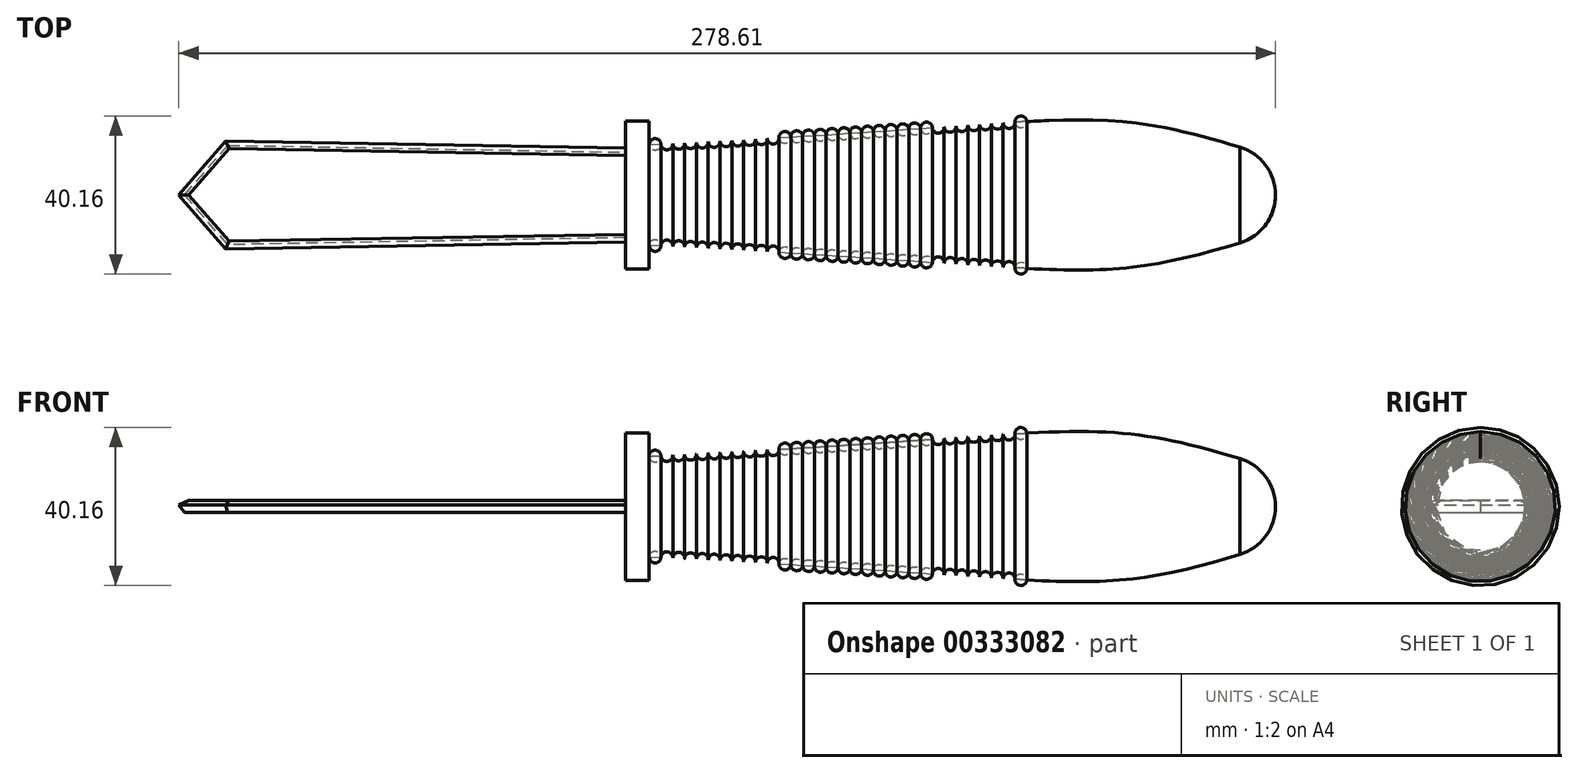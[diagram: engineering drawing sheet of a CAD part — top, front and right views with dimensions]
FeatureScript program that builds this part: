
annotation { "Feature Type Name" : "Feature", "Feature Type Description" : "" }
export const myFeature = defineFeature(function(context is Context, id is Id, definition is map)
    precondition{}
    {
        {
            var Q0;
            Q0=qCreatedBy(makeId("Top.planeOp"),FACE);
            var sketch = newSketch(context, id + "F0", { "sketchPlane" : qUnion([Q0])});
            skLineSegment(sketch, "E0", {"start": v(0, 0) * mm, "end": v(0, -18.75) * mm});
            skLineSegment(sketch, "E1", {"start": v(0, -18.75) * mm, "end": v(6, -18.75) * mm});
            skLineSegment(sketch, "E2", {"start": v(6, -18.75) * mm, "end": v(6, -12.75) * mm});
            skArc(sketch, "E3", {"start": v(156.05, -12.16) * mm, "mid": v(162.59, -7.58) * mm, "end": v(165.1, 0) * mm});
            skFitSpline(sketch, "E4", {"points": [v(6, -12.75) * mm, v(156.05, -12.16) * mm, v(257.66, 24.42) * mm], "startDerivative": vector(616.47, -30.16) * mm, "endDerivative": vector(40.55, 25.58) * mm});
            skLineSegment(sketch, "E5", {"start": v(0, 0) * mm, "end": v(152.4, 0) * mm});
            skCircle(sketch, "E6", {"center": v(7.5, -12.82) * mm, "radius": 1.5 * mm});
            skCircle(sketch, "E7", {"center": v(10.5, -12.97) * mm, "radius": 1.5 * mm});
            skCircle(sketch, "E8", {"center": v(13.5, -13.13) * mm, "radius": 1.5 * mm});
            skCircle(sketch, "E9", {"center": v(16.5, -13.28) * mm, "radius": 1.5 * mm});
            skCircle(sketch, "E10", {"center": v(19.5, -13.44) * mm, "radius": 1.5 * mm});
            skCircle(sketch, "E11", {"center": v(22.5, -13.6) * mm, "radius": 1.5 * mm});
            skLineSegment(sketch, "E12", {"start": v(152.4, 0) * mm, "end": v(165.1, 0) * mm});
            skLineSegment(sketch, "E13", {"start": v(7.5, -12.82) * mm, "end": v(10.5, -12.97) * mm, "construction": true});
            skLineSegment(sketch, "E14", {"start": v(10.5, -12.97) * mm, "end": v(13.5, -13.13) * mm, "construction": true});
            skLineSegment(sketch, "E15", {"start": v(13.5, -13.13) * mm, "end": v(16.5, -13.28) * mm, "construction": true});
            skLineSegment(sketch, "E16", {"start": v(16.5, -13.28) * mm, "end": v(19.5, -13.44) * mm, "construction": true});
            skLineSegment(sketch, "E17", {"start": v(19.5, -13.44) * mm, "end": v(22.5, -13.6) * mm, "construction": true});
            skCircle(sketch, "E18", {"center": v(28.5, -13.93) * mm, "radius": 1.5 * mm});
            skCircle(sketch, "E19", {"center": v(31.5, -14.1) * mm, "radius": 1.5 * mm});
            skCircle(sketch, "E20", {"center": v(25.5, -13.77) * mm, "radius": 1.5 * mm});
            skCircle(sketch, "E21", {"center": v(34.5, -14.28) * mm, "radius": 1.5 * mm});
            skCircle(sketch, "E22", {"center": v(37.5, -14.45) * mm, "radius": 1.5 * mm});
            skCircle(sketch, "E23", {"center": v(40.49, -14.63) * mm, "radius": 1.5 * mm});
            skCircle(sketch, "E24", {"center": v(43.49, -14.82) * mm, "radius": 1.5 * mm});
            skCircle(sketch, "E25", {"center": v(46.49, -15) * mm, "radius": 1.5 * mm});
            skCircle(sketch, "E26", {"center": v(49.48, -15.2) * mm, "radius": 1.5 * mm});
            skCircle(sketch, "E27", {"center": v(52.48, -15.38) * mm, "radius": 1.5 * mm});
            skCircle(sketch, "E28", {"center": v(55.48, -15.58) * mm, "radius": 1.5 * mm});
            skLineSegment(sketch, "E29", {"start": v(22.5, -13.6) * mm, "end": v(25.5, -13.77) * mm, "construction": true});
            skLineSegment(sketch, "E30", {"start": v(25.5, -13.77) * mm, "end": v(28.5, -13.93) * mm, "construction": true});
            skLineSegment(sketch, "E31", {"start": v(28.5, -13.93) * mm, "end": v(31.5, -14.1) * mm, "construction": true});
            skLineSegment(sketch, "E32", {"start": v(31.5, -14.1) * mm, "end": v(34.5, -14.28) * mm, "construction": true});
            skLineSegment(sketch, "E33", {"start": v(34.5, -14.28) * mm, "end": v(37.5, -14.45) * mm, "construction": true});
            skLineSegment(sketch, "E34", {"start": v(37.5, -14.45) * mm, "end": v(40.49, -14.63) * mm, "construction": true});
            skLineSegment(sketch, "E35", {"start": v(40.49, -14.63) * mm, "end": v(43.49, -14.82) * mm, "construction": true});
            skLineSegment(sketch, "E36", {"start": v(43.49, -14.82) * mm, "end": v(46.49, -15) * mm, "construction": true});
            skLineSegment(sketch, "E37", {"start": v(52.48, -15.38) * mm, "end": v(55.48, -15.58) * mm, "construction": true});
            skLineSegment(sketch, "E38", {"start": v(52.48, -15.38) * mm, "end": v(49.48, -15.2) * mm, "construction": true});
            skLineSegment(sketch, "E39", {"start": v(49.48, -15.2) * mm, "end": v(46.49, -15) * mm, "construction": true});
            skCircle(sketch, "E40", {"center": v(58.48, -15.77) * mm, "radius": 1.5 * mm});
            skCircle(sketch, "E41", {"center": v(61.47, -15.97) * mm, "radius": 1.5 * mm});
            skCircle(sketch, "E42", {"center": v(64.47, -16.18) * mm, "radius": 1.5 * mm});
            skCircle(sketch, "E43", {"center": v(67.47, -16.38) * mm, "radius": 1.5 * mm});
            skCircle(sketch, "E44", {"center": v(70.46, -16.59) * mm, "radius": 1.5 * mm});
            skLineSegment(sketch, "E45", {"start": v(55.48, -15.58) * mm, "end": v(58.48, -15.77) * mm, "construction": true});
            skLineSegment(sketch, "E46", {"start": v(58.48, -15.77) * mm, "end": v(61.47, -15.97) * mm, "construction": true});
            skLineSegment(sketch, "E47", {"start": v(61.47, -15.97) * mm, "end": v(64.47, -16.18) * mm, "construction": true});
            skLineSegment(sketch, "E48", {"start": v(64.47, -16.18) * mm, "end": v(67.47, -16.38) * mm, "construction": true});
            skLineSegment(sketch, "E49", {"start": v(67.47, -16.38) * mm, "end": v(70.46, -16.59) * mm, "construction": true});
            skCircle(sketch, "E50", {"center": v(73.46, -16.8) * mm, "radius": 1.5 * mm});
            skCircle(sketch, "E51", {"center": v(76.46, -17) * mm, "radius": 1.5 * mm});
            skCircle(sketch, "E52", {"center": v(79.45, -17.21) * mm, "radius": 1.5 * mm});
            skCircle(sketch, "E53", {"center": v(82.45, -17.42) * mm, "radius": 1.5 * mm});
            skCircle(sketch, "E54", {"center": v(85.45, -17.63) * mm, "radius": 1.5 * mm});
            skCircle(sketch, "E55", {"center": v(88.44, -17.83) * mm, "radius": 1.5 * mm});
            skCircle(sketch, "E56", {"center": v(91.44, -18.03) * mm, "radius": 1.5 * mm});
            skCircle(sketch, "E57", {"center": v(94.44, -18.22) * mm, "radius": 1.5 * mm});
            skLineSegment(sketch, "E58", {"start": v(70.46, -16.59) * mm, "end": v(73.46, -16.8) * mm, "construction": true});
            skLineSegment(sketch, "E59", {"start": v(73.46, -16.8) * mm, "end": v(76.46, -17) * mm, "construction": true});
            skLineSegment(sketch, "E60", {"start": v(76.46, -17) * mm, "end": v(79.45, -17.21) * mm, "construction": true});
            skLineSegment(sketch, "E61", {"start": v(79.45, -17.21) * mm, "end": v(82.45, -17.42) * mm, "construction": true});
            skLineSegment(sketch, "E62", {"start": v(82.45, -17.42) * mm, "end": v(85.45, -17.63) * mm, "construction": true});
            skLineSegment(sketch, "E63", {"start": v(85.45, -17.63) * mm, "end": v(88.44, -17.83) * mm, "construction": true});
            skLineSegment(sketch, "E64", {"start": v(88.44, -17.83) * mm, "end": v(91.44, -18.03) * mm, "construction": true});
            skLineSegment(sketch, "E65", {"start": v(91.44, -18.03) * mm, "end": v(94.44, -18.22) * mm, "construction": true});
            skCircle(sketch, "E66", {"center": v(97.44, -18.4) * mm, "radius": 1.5 * mm});
            skCircle(sketch, "E67", {"center": v(100.43, -18.58) * mm, "radius": 1.5 * mm});
            skLineSegment(sketch, "E68", {"start": v(94.44, -18.22) * mm, "end": v(97.44, -18.4) * mm, "construction": true});
            skLineSegment(sketch, "E69", {"start": v(97.44, -18.4) * mm, "end": v(100.43, -18.58) * mm, "construction": true});
            skSolve(sketch);
        }
        {
            var Q0;
            Q0=makeQuery(id+"F0.imprint","IMPRINT",FACE,{"disambiguationData":[TD([[makeQuery(id+"F0.imprint","IMPRINT",EDGE,{"derivedFrom":sQuery(id+"F0.wireOp",EDGE,"E0")}),1.0]])]});
            var Q1;
            {var subQ0=sQuery(id+"F0.wireOp",EDGE,"E10");var subQ1=sQuery(id+"F0.wireOp",EDGE,"E4");var subQ2=makeQuery(id+"F0.imprint","INTERSECT",VERTEX,{"disambiguationData":[OD(0.0)],"derivedFrom":[subQ1,subQ0]});Q1=makeQuery(id+"F0.imprint","IMPRINT",FACE,{"disambiguationData":[TD([[makeQuery(id+"F0.imprint","IMPRINT",EDGE,{"disambiguationData":[TD([[subQ2,-1.0]])],"derivedFrom":subQ1}),-1.0]])]});}
            var Q2;
            {var subQ0=sQuery(id+"F0.wireOp",EDGE,"E10");var subQ1=sQuery(id+"F0.wireOp",EDGE,"E4");var subQ2=makeQuery(id+"F0.imprint","INTERSECT",VERTEX,{"disambiguationData":[OD(0.0)],"derivedFrom":[subQ1,subQ0]});Q2=makeQuery(id+"F0.imprint","IMPRINT",FACE,{"disambiguationData":[TD([[makeQuery(id+"F0.imprint","IMPRINT",EDGE,{"disambiguationData":[TD([[subQ2,-1.0]])],"derivedFrom":subQ1}),1.0]])]});}
            var Q3;
            {var subQ0=sQuery(id+"F0.wireOp",EDGE,"E11");var subQ1=sQuery(id+"F0.wireOp",EDGE,"E4");var subQ2=makeQuery(id+"F0.imprint","INTERSECT",VERTEX,{"disambiguationData":[OD(0.0)],"derivedFrom":[subQ1,subQ0]});Q3=makeQuery(id+"F0.imprint","IMPRINT",FACE,{"disambiguationData":[TD([[makeQuery(id+"F0.imprint","IMPRINT",EDGE,{"disambiguationData":[TD([[subQ2,-1.0]])],"derivedFrom":subQ1}),-1.0]])]});}
            var Q4;
            {var subQ0=sQuery(id+"F0.wireOp",EDGE,"E9");var subQ1=sQuery(id+"F0.wireOp",EDGE,"E4");var subQ2=makeQuery(id+"F0.imprint","INTERSECT",VERTEX,{"disambiguationData":[OD(0.0)],"derivedFrom":[subQ1,subQ0]});Q4=makeQuery(id+"F0.imprint","IMPRINT",FACE,{"disambiguationData":[TD([[makeQuery(id+"F0.imprint","IMPRINT",EDGE,{"disambiguationData":[TD([[subQ2,-1.0]])],"derivedFrom":subQ1}),-1.0]])]});}
            var Q5;
            {var subQ0=sQuery(id+"F0.wireOp",EDGE,"E8");var subQ1=sQuery(id+"F0.wireOp",EDGE,"E4");var subQ2=makeQuery(id+"F0.imprint","INTERSECT",VERTEX,{"disambiguationData":[OD(0.0)],"derivedFrom":[subQ1,subQ0]});Q5=makeQuery(id+"F0.imprint","IMPRINT",FACE,{"disambiguationData":[TD([[makeQuery(id+"F0.imprint","IMPRINT",EDGE,{"disambiguationData":[TD([[subQ2,-1.0]])],"derivedFrom":subQ1}),-1.0]])]});}
            var Q6;
            {var subQ0=sQuery(id+"F0.wireOp",EDGE,"E6");var subQ2=sQuery(id+"F0.wireOp",EDGE,"E2");var subQ4=makeQuery(id+"F0.imprint","INTERSECT",VERTEX,{"derivedFrom":[subQ2,subQ0]});Q6=makeQuery(id+"F0.imprint","IMPRINT",FACE,{"disambiguationData":[TD([[makeQuery(id+"F0.imprint","IMPRINT",EDGE,{"disambiguationData":[TD([[subQ4,-1.0]])],"derivedFrom":subQ0}),1.0]])]});}
            var Q7;
            {var subQ0=sQuery(id+"F0.wireOp",EDGE,"E7");var subQ1=sQuery(id+"F0.wireOp",EDGE,"E4");var subQ2=makeQuery(id+"F0.imprint","INTERSECT",VERTEX,{"disambiguationData":[OD(0.0)],"derivedFrom":[subQ1,subQ0]});Q7=makeQuery(id+"F0.imprint","IMPRINT",FACE,{"disambiguationData":[TD([[makeQuery(id+"F0.imprint","IMPRINT",EDGE,{"disambiguationData":[TD([[subQ2,-1.0]])],"derivedFrom":subQ1}),-1.0]])]});}
            var Q8;
            {var subQ0=sQuery(id+"F0.wireOp",EDGE,"E20");var subQ1=sQuery(id+"F0.wireOp",EDGE,"E4");var subQ2=makeQuery(id+"F0.imprint","INTERSECT",VERTEX,{"disambiguationData":[OD(0.0)],"derivedFrom":[subQ1,subQ0]});Q8=makeQuery(id+"F0.imprint","IMPRINT",FACE,{"disambiguationData":[TD([[makeQuery(id+"F0.imprint","IMPRINT",EDGE,{"disambiguationData":[TD([[subQ2,-1.0]])],"derivedFrom":subQ1}),-1.0]])]});}
            var Q9;
            {var subQ0=sQuery(id+"F0.wireOp",EDGE,"E18");var subQ1=sQuery(id+"F0.wireOp",EDGE,"E4");var subQ2=makeQuery(id+"F0.imprint","INTERSECT",VERTEX,{"disambiguationData":[OD(0.0)],"derivedFrom":[subQ1,subQ0]});Q9=makeQuery(id+"F0.imprint","IMPRINT",FACE,{"disambiguationData":[TD([[makeQuery(id+"F0.imprint","IMPRINT",EDGE,{"disambiguationData":[TD([[subQ2,-1.0]])],"derivedFrom":subQ1}),-1.0]])]});}
            var Q10;
            {var subQ0=sQuery(id+"F0.wireOp",EDGE,"E19");var subQ1=sQuery(id+"F0.wireOp",EDGE,"E4");var subQ2=makeQuery(id+"F0.imprint","INTERSECT",VERTEX,{"disambiguationData":[OD(0.0)],"derivedFrom":[subQ1,subQ0]});Q10=makeQuery(id+"F0.imprint","IMPRINT",FACE,{"disambiguationData":[TD([[makeQuery(id+"F0.imprint","IMPRINT",EDGE,{"disambiguationData":[TD([[subQ2,-1.0]])],"derivedFrom":subQ1}),-1.0]])]});}
            var Q11;
            {var subQ0=sQuery(id+"F0.wireOp",EDGE,"E21");var subQ1=sQuery(id+"F0.wireOp",EDGE,"E4");var subQ2=makeQuery(id+"F0.imprint","INTERSECT",VERTEX,{"disambiguationData":[OD(0.0)],"derivedFrom":[subQ1,subQ0]});Q11=makeQuery(id+"F0.imprint","IMPRINT",FACE,{"disambiguationData":[TD([[makeQuery(id+"F0.imprint","IMPRINT",EDGE,{"disambiguationData":[TD([[subQ2,-1.0]])],"derivedFrom":subQ1}),-1.0]])]});}
            var Q12;
            {var subQ0=sQuery(id+"F0.wireOp",EDGE,"E22");var subQ1=sQuery(id+"F0.wireOp",EDGE,"E4");var subQ2=makeQuery(id+"F0.imprint","INTERSECT",VERTEX,{"disambiguationData":[OD(0.0)],"derivedFrom":[subQ1,subQ0]});Q12=makeQuery(id+"F0.imprint","IMPRINT",FACE,{"disambiguationData":[TD([[makeQuery(id+"F0.imprint","IMPRINT",EDGE,{"disambiguationData":[TD([[subQ2,-1.0]])],"derivedFrom":subQ1}),-1.0]])]});}
            var Q13;
            {var subQ0=sQuery(id+"F0.wireOp",EDGE,"E23");var subQ1=sQuery(id+"F0.wireOp",EDGE,"E4");var subQ2=makeQuery(id+"F0.imprint","INTERSECT",VERTEX,{"disambiguationData":[OD(0.0)],"derivedFrom":[subQ1,subQ0]});Q13=makeQuery(id+"F0.imprint","IMPRINT",FACE,{"disambiguationData":[TD([[makeQuery(id+"F0.imprint","IMPRINT",EDGE,{"disambiguationData":[TD([[subQ2,-1.0]])],"derivedFrom":subQ1}),-1.0]])]});}
            var Q14;
            {var subQ0=sQuery(id+"F0.wireOp",EDGE,"E24");var subQ1=sQuery(id+"F0.wireOp",EDGE,"E4");var subQ2=makeQuery(id+"F0.imprint","INTERSECT",VERTEX,{"disambiguationData":[OD(0.0)],"derivedFrom":[subQ1,subQ0]});Q14=makeQuery(id+"F0.imprint","IMPRINT",FACE,{"disambiguationData":[TD([[makeQuery(id+"F0.imprint","IMPRINT",EDGE,{"disambiguationData":[TD([[subQ2,-1.0]])],"derivedFrom":subQ1}),-1.0]])]});}
            var Q15;
            {var subQ0=sQuery(id+"F0.wireOp",EDGE,"E25");var subQ1=sQuery(id+"F0.wireOp",EDGE,"E4");var subQ2=makeQuery(id+"F0.imprint","INTERSECT",VERTEX,{"disambiguationData":[OD(0.0)],"derivedFrom":[subQ1,subQ0]});Q15=makeQuery(id+"F0.imprint","IMPRINT",FACE,{"disambiguationData":[TD([[makeQuery(id+"F0.imprint","IMPRINT",EDGE,{"disambiguationData":[TD([[subQ2,-1.0]])],"derivedFrom":subQ1}),-1.0]])]});}
            var Q16;
            {var subQ0=sQuery(id+"F0.wireOp",EDGE,"E26");var subQ1=sQuery(id+"F0.wireOp",EDGE,"E4");var subQ2=makeQuery(id+"F0.imprint","INTERSECT",VERTEX,{"disambiguationData":[OD(0.0)],"derivedFrom":[subQ1,subQ0]});Q16=makeQuery(id+"F0.imprint","IMPRINT",FACE,{"disambiguationData":[TD([[makeQuery(id+"F0.imprint","IMPRINT",EDGE,{"disambiguationData":[TD([[subQ2,-1.0]])],"derivedFrom":subQ1}),-1.0]])]});}
            var Q17;
            {var subQ0=sQuery(id+"F0.wireOp",EDGE,"E27");var subQ1=sQuery(id+"F0.wireOp",EDGE,"E4");var subQ2=makeQuery(id+"F0.imprint","INTERSECT",VERTEX,{"disambiguationData":[OD(0.0)],"derivedFrom":[subQ1,subQ0]});Q17=makeQuery(id+"F0.imprint","IMPRINT",FACE,{"disambiguationData":[TD([[makeQuery(id+"F0.imprint","IMPRINT",EDGE,{"disambiguationData":[TD([[subQ2,-1.0]])],"derivedFrom":subQ1}),-1.0]])]});}
            var Q18;
            {var subQ0=sQuery(id+"F0.wireOp",EDGE,"E28");var subQ1=sQuery(id+"F0.wireOp",EDGE,"E4");var subQ2=makeQuery(id+"F0.imprint","INTERSECT",VERTEX,{"disambiguationData":[OD(0.0)],"derivedFrom":[subQ1,subQ0]});Q18=makeQuery(id+"F0.imprint","IMPRINT",FACE,{"disambiguationData":[TD([[makeQuery(id+"F0.imprint","IMPRINT",EDGE,{"disambiguationData":[TD([[subQ2,-1.0]])],"derivedFrom":subQ1}),-1.0]])]});}
            var Q19;
            {var subQ0=sQuery(id+"F0.wireOp",EDGE,"E40");var subQ1=sQuery(id+"F0.wireOp",EDGE,"E4");var subQ2=makeQuery(id+"F0.imprint","INTERSECT",VERTEX,{"disambiguationData":[OD(0.0)],"derivedFrom":[subQ1,subQ0]});Q19=makeQuery(id+"F0.imprint","IMPRINT",FACE,{"disambiguationData":[TD([[makeQuery(id+"F0.imprint","IMPRINT",EDGE,{"disambiguationData":[TD([[subQ2,-1.0]])],"derivedFrom":subQ1}),-1.0]])]});}
            var Q20;
            {var subQ0=sQuery(id+"F0.wireOp",EDGE,"E41");var subQ1=sQuery(id+"F0.wireOp",EDGE,"E4");var subQ2=makeQuery(id+"F0.imprint","INTERSECT",VERTEX,{"disambiguationData":[OD(0.0)],"derivedFrom":[subQ1,subQ0]});Q20=makeQuery(id+"F0.imprint","IMPRINT",FACE,{"disambiguationData":[TD([[makeQuery(id+"F0.imprint","IMPRINT",EDGE,{"disambiguationData":[TD([[subQ2,-1.0]])],"derivedFrom":subQ1}),-1.0]])]});}
            var Q21;
            {var subQ0=sQuery(id+"F0.wireOp",EDGE,"E42");var subQ1=sQuery(id+"F0.wireOp",EDGE,"E4");var subQ2=makeQuery(id+"F0.imprint","INTERSECT",VERTEX,{"disambiguationData":[OD(0.0)],"derivedFrom":[subQ1,subQ0]});Q21=makeQuery(id+"F0.imprint","IMPRINT",FACE,{"disambiguationData":[TD([[makeQuery(id+"F0.imprint","IMPRINT",EDGE,{"disambiguationData":[TD([[subQ2,-1.0]])],"derivedFrom":subQ1}),-1.0]])]});}
            var Q22;
            {var subQ0=sQuery(id+"F0.wireOp",EDGE,"E43");var subQ1=sQuery(id+"F0.wireOp",EDGE,"E4");var subQ2=makeQuery(id+"F0.imprint","INTERSECT",VERTEX,{"disambiguationData":[OD(0.0)],"derivedFrom":[subQ1,subQ0]});Q22=makeQuery(id+"F0.imprint","IMPRINT",FACE,{"disambiguationData":[TD([[makeQuery(id+"F0.imprint","IMPRINT",EDGE,{"disambiguationData":[TD([[subQ2,-1.0]])],"derivedFrom":subQ1}),-1.0]])]});}
            var Q23;
            {var subQ0=sQuery(id+"F0.wireOp",EDGE,"E44");var subQ1=sQuery(id+"F0.wireOp",EDGE,"E4");var subQ2=makeQuery(id+"F0.imprint","INTERSECT",VERTEX,{"disambiguationData":[OD(0.0)],"derivedFrom":[subQ1,subQ0]});Q23=makeQuery(id+"F0.imprint","IMPRINT",FACE,{"disambiguationData":[TD([[makeQuery(id+"F0.imprint","IMPRINT",EDGE,{"disambiguationData":[TD([[subQ2,-1.0]])],"derivedFrom":subQ1}),-1.0]])]});}
            var Q24;
            {var subQ0=sQuery(id+"F0.wireOp",EDGE,"E50");var subQ1=sQuery(id+"F0.wireOp",EDGE,"E4");var subQ2=makeQuery(id+"F0.imprint","INTERSECT",VERTEX,{"disambiguationData":[OD(0.0)],"derivedFrom":[subQ1,subQ0]});Q24=makeQuery(id+"F0.imprint","IMPRINT",FACE,{"disambiguationData":[TD([[makeQuery(id+"F0.imprint","IMPRINT",EDGE,{"disambiguationData":[TD([[subQ2,-1.0]])],"derivedFrom":subQ1}),-1.0]])]});}
            var Q25;
            {var subQ0=sQuery(id+"F0.wireOp",EDGE,"E51");var subQ1=sQuery(id+"F0.wireOp",EDGE,"E4");var subQ2=makeQuery(id+"F0.imprint","INTERSECT",VERTEX,{"disambiguationData":[OD(0.0)],"derivedFrom":[subQ1,subQ0]});Q25=makeQuery(id+"F0.imprint","IMPRINT",FACE,{"disambiguationData":[TD([[makeQuery(id+"F0.imprint","IMPRINT",EDGE,{"disambiguationData":[TD([[subQ2,-1.0]])],"derivedFrom":subQ1}),-1.0]])]});}
            var Q26;
            {var subQ0=sQuery(id+"F0.wireOp",EDGE,"E52");var subQ1=sQuery(id+"F0.wireOp",EDGE,"E4");var subQ2=makeQuery(id+"F0.imprint","INTERSECT",VERTEX,{"disambiguationData":[OD(0.0)],"derivedFrom":[subQ1,subQ0]});Q26=makeQuery(id+"F0.imprint","IMPRINT",FACE,{"disambiguationData":[TD([[makeQuery(id+"F0.imprint","IMPRINT",EDGE,{"disambiguationData":[TD([[subQ2,-1.0]])],"derivedFrom":subQ1}),-1.0]])]});}
            var Q27;
            {var subQ0=sQuery(id+"F0.wireOp",EDGE,"E54");var subQ1=sQuery(id+"F0.wireOp",EDGE,"E4");var subQ2=makeQuery(id+"F0.imprint","INTERSECT",VERTEX,{"disambiguationData":[OD(0.0)],"derivedFrom":[subQ1,subQ0]});Q27=makeQuery(id+"F0.imprint","IMPRINT",FACE,{"disambiguationData":[TD([[makeQuery(id+"F0.imprint","IMPRINT",EDGE,{"disambiguationData":[TD([[subQ2,-1.0]])],"derivedFrom":subQ1}),-1.0]])]});}
            var Q28;
            {var subQ0=sQuery(id+"F0.wireOp",EDGE,"E53");var subQ1=sQuery(id+"F0.wireOp",EDGE,"E4");var subQ2=makeQuery(id+"F0.imprint","INTERSECT",VERTEX,{"disambiguationData":[OD(0.0)],"derivedFrom":[subQ1,subQ0]});Q28=makeQuery(id+"F0.imprint","IMPRINT",FACE,{"disambiguationData":[TD([[makeQuery(id+"F0.imprint","IMPRINT",EDGE,{"disambiguationData":[TD([[subQ2,-1.0]])],"derivedFrom":subQ1}),-1.0]])]});}
            var Q29;
            {var subQ0=sQuery(id+"F0.wireOp",EDGE,"E55");var subQ1=sQuery(id+"F0.wireOp",EDGE,"E4");var subQ2=makeQuery(id+"F0.imprint","INTERSECT",VERTEX,{"disambiguationData":[OD(0.0)],"derivedFrom":[subQ1,subQ0]});Q29=makeQuery(id+"F0.imprint","IMPRINT",FACE,{"disambiguationData":[TD([[makeQuery(id+"F0.imprint","IMPRINT",EDGE,{"disambiguationData":[TD([[subQ2,-1.0]])],"derivedFrom":subQ1}),-1.0]])]});}
            var Q30;
            {var subQ0=sQuery(id+"F0.wireOp",EDGE,"E56");var subQ1=sQuery(id+"F0.wireOp",EDGE,"E4");var subQ2=makeQuery(id+"F0.imprint","INTERSECT",VERTEX,{"disambiguationData":[OD(0.0)],"derivedFrom":[subQ1,subQ0]});Q30=makeQuery(id+"F0.imprint","IMPRINT",FACE,{"disambiguationData":[TD([[makeQuery(id+"F0.imprint","IMPRINT",EDGE,{"disambiguationData":[TD([[subQ2,-1.0]])],"derivedFrom":subQ1}),-1.0]])]});}
            var Q31;
            {var subQ0=sQuery(id+"F0.wireOp",EDGE,"E57");var subQ1=sQuery(id+"F0.wireOp",EDGE,"E4");var subQ2=makeQuery(id+"F0.imprint","INTERSECT",VERTEX,{"disambiguationData":[OD(0.0)],"derivedFrom":[subQ1,subQ0]});Q31=makeQuery(id+"F0.imprint","IMPRINT",FACE,{"disambiguationData":[TD([[makeQuery(id+"F0.imprint","IMPRINT",EDGE,{"disambiguationData":[TD([[subQ2,-1.0]])],"derivedFrom":subQ1}),-1.0]])]});}
            var Q32;
            {var subQ0=sQuery(id+"F0.wireOp",EDGE,"E66");var subQ1=sQuery(id+"F0.wireOp",EDGE,"E4");var subQ2=makeQuery(id+"F0.imprint","INTERSECT",VERTEX,{"disambiguationData":[OD(0.0)],"derivedFrom":[subQ1,subQ0]});Q32=makeQuery(id+"F0.imprint","IMPRINT",FACE,{"disambiguationData":[TD([[makeQuery(id+"F0.imprint","IMPRINT",EDGE,{"disambiguationData":[TD([[subQ2,-1.0]])],"derivedFrom":subQ1}),-1.0]])]});}
            var Q33;
            {var subQ0=sQuery(id+"F0.wireOp",EDGE,"E67");var subQ1=sQuery(id+"F0.wireOp",EDGE,"E4");var subQ2=makeQuery(id+"F0.imprint","INTERSECT",VERTEX,{"disambiguationData":[OD(0.0)],"derivedFrom":[subQ1,subQ0]});Q33=makeQuery(id+"F0.imprint","IMPRINT",FACE,{"disambiguationData":[TD([[makeQuery(id+"F0.imprint","IMPRINT",EDGE,{"disambiguationData":[TD([[subQ2,-1.0]])],"derivedFrom":subQ1}),-1.0]])]});}
            var Q34;
            Q34=sQuery(id+"F0.wireOp",EDGE,"E5");
            revolve(context, id + "F1", {"entities" : qUnion([Q0, Q1, Q2, Q3, Q4, Q5, Q6, Q7, Q8, Q9, Q10, Q11, Q12, Q13, Q14, Q15, Q16, Q17, Q18, Q19, Q20, Q21, Q22, Q23, Q24, Q25, Q26, Q27, Q28, Q29, Q30, Q31, Q32, Q33]), "axis" : qUnion([Q34]), "revolveType" : RevolveType.FULL});
        }
        {
            var Q0;
            Q0=qCreatedBy(makeId("Top.planeOp"),FACE);
            var sketch = newSketch(context, id + "F2", { "sketchPlane" : qUnion([Q0])});
            skLineSegment(sketch, "E70", {"start": v(0, -12) * mm, "end": v(-101.6, -13.77) * mm});
            skLineSegment(sketch, "E71", {"start": v(-101.6, -13.77) * mm, "end": v(-113.6, 0) * mm});
            skLineSegment(sketch, "E72.MirrorCS", {"start": v(0, 12) * mm, "end": v(-101.6, 13.77) * mm});
            skLineSegment(sketch, "E73.MirrorCS", {"start": v(-101.6, 13.77) * mm, "end": v(-113.6, 0) * mm});
            skLineSegment(sketch, "E74", {"start": v(0, -12) * mm, "end": v(0, 12) * mm});
            skSolve(sketch);
        }
        {
            var Q0;
            Q0 = qSketchRegion(id + "F2", true);
            extrude(context, id + "F3", {"entities" : qUnion([Q0]), "endBound" : BoundingType.SYMMETRIC, "depth" : 3 * mm});
        }
        {
            var Q0;
            Q0=makeQuery(id+"F3.opExtrude","CAP_EDGE",EDGE,{"disambiguationData":[OSD([sQuery(id+"F2.wireOp",EDGE,"E72.MirrorCS")])],"isStart":false});
            var Q1;
            Q1=makeQuery(id+"F3.opExtrude","CAP_EDGE",EDGE,{"disambiguationData":[OSD([sQuery(id+"F2.wireOp",EDGE,"E73.MirrorCS")])],"isStart":false});
            var Q2;
            Q2=makeQuery(id+"F3.opExtrude","CAP_EDGE",EDGE,{"disambiguationData":[OSD([sQuery(id+"F2.wireOp",EDGE,"E71")])],"isStart":false});
            var Q3;
            Q3=makeQuery(id+"F3.opExtrude","CAP_EDGE",EDGE,{"disambiguationData":[OSD([sQuery(id+"F2.wireOp",EDGE,"E70")])],"isStart":false});
            chamfer(context, id + "F4", {"entities" : qUnion([Q0, Q1, Q2, Q3]), "chamferType" : ChamferType.OFFSET_ANGLE, "width" : 2 * mm, "oppositeDirection" : false, "angle" : 30 * degree, "tangentPropagation" : true});
        }
        {
            var Q0;
            Q0=makeQuery(id+"F3.opExtrude","CAP_EDGE",EDGE,{"disambiguationData":[OSD([sQuery(id+"F2.wireOp",EDGE,"E72.MirrorCS")])],"isStart":true});
            var Q1;
            Q1=makeQuery(id+"F3.opExtrude","CAP_EDGE",EDGE,{"disambiguationData":[OSD([sQuery(id+"F2.wireOp",EDGE,"E73.MirrorCS")])],"isStart":true});
            var Q2;
            Q2=makeQuery(id+"F3.opExtrude","CAP_EDGE",EDGE,{"disambiguationData":[OSD([sQuery(id+"F2.wireOp",EDGE,"E71")])],"isStart":true});
            var Q3;
            Q3=makeQuery(id+"F3.opExtrude","CAP_EDGE",EDGE,{"disambiguationData":[OSD([sQuery(id+"F2.wireOp",EDGE,"E70")])],"isStart":true});
            chamfer(context, id + "F5", {"entities" : qUnion([Q0, Q1, Q2, Q3]), "chamferType" : ChamferType.OFFSET_ANGLE, "width" : 2 * mm, "oppositeDirection" : false, "angle" : 30 * degree, "tangentPropagation" : true});
        }
    });
